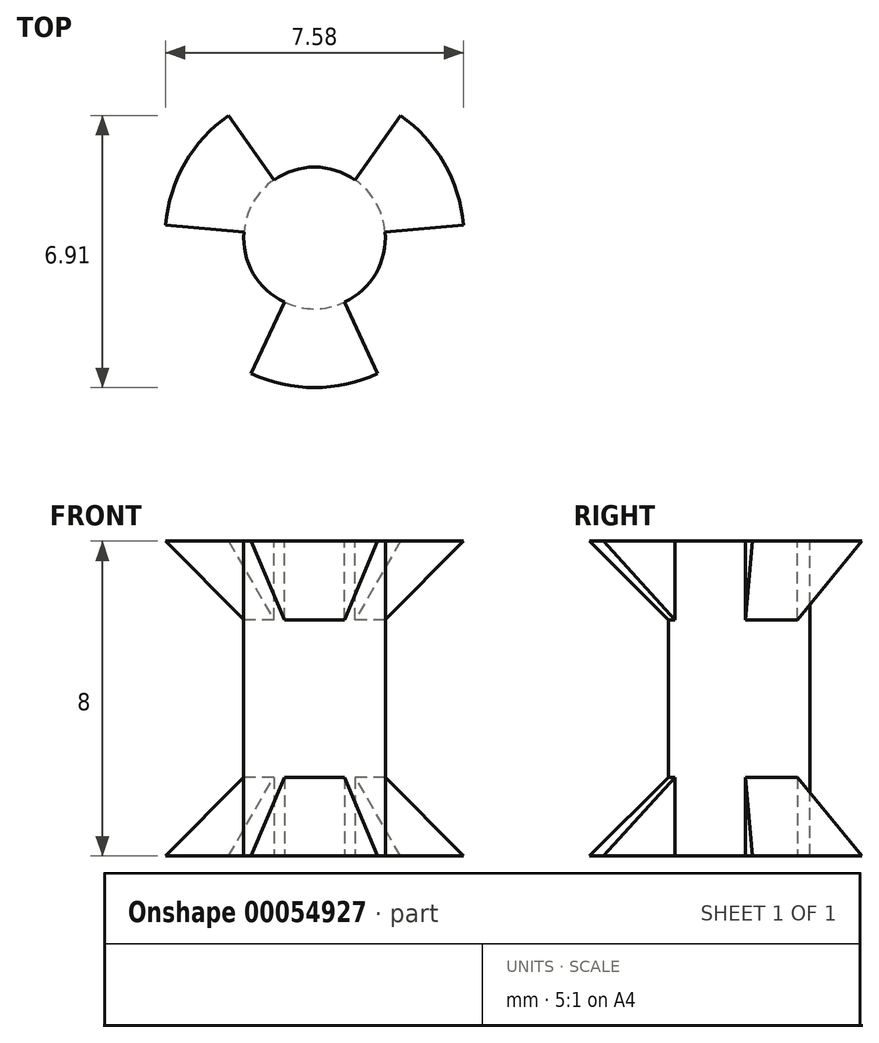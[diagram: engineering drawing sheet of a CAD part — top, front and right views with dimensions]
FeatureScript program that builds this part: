
annotation { "Feature Type Name" : "Feature", "Feature Type Description" : "" }
export const myFeature = defineFeature(function(context is Context, id is Id, definition is map)
    precondition{}
    {
        {
            var Q0;
            Q0=qCreatedBy(makeId("Front.planeOp"),FACE);
            var sketch = newSketch(context, id + "F0", { "sketchPlane" : qUnion([Q0])});
            skLineSegment(sketch, "E0", {"start": v(-1.8, 4) * mm, "end": v(-1.8, 0) * mm});
            skLineSegment(sketch, "E1", {"start": v(-1.8, 4) * mm, "end": v(0, 4) * mm});
            skLineSegment(sketch, "E2", {"start": v(0, 4) * mm, "end": v(0, 0) * mm});
            skLineSegment(sketch, "E3", {"start": v(0, 0) * mm, "end": v(-1.8, 0) * mm});
            skLineSegment(sketch, "E4", {"start": v(-1.8, 0) * mm, "end": v(-3.8, 0) * mm});
            skLineSegment(sketch, "E5", {"start": v(-3.8, 0) * mm, "end": v(-1.8, 2) * mm});
            skPoint(sketch, "E6", {"position": v(-1.8, 2) * mm});
            skSolve(sketch);
        }
        {
            var Q0;
            {var subQ0=sQuery(id+"F0.wireOp",EDGE,"E4");Q0=makeQuery(id+"F0.imprint","IMPRINT",FACE,{"disambiguationData":[TD([[makeQuery(id+"F0.imprint","IMPRINT",EDGE,{"derivedFrom":subQ0}),-1.0]])]});}
            var Q1;
            {var subQ0=sQuery(id+"F0.wireOp",EDGE,"E1");Q1=makeQuery(id+"F0.imprint","IMPRINT",FACE,{"disambiguationData":[TD([[makeQuery(id+"F0.imprint","IMPRINT",EDGE,{"derivedFrom":subQ0}),-1.0]])]});}
            var Q2;
            Q2=sQuery(id+"F0.wireOp",EDGE,"E2");
            revolve(context, id + "F1", {"entities" : qUnion([Q0, Q1]), "axis" : qUnion([Q2]), "revolveType" : RevolveType.FULL});
        }
        {
            var Q0;
            Q0=makeQuery(id+"F1.opRevolve","SWEPT_FACE",FACE,{"disambiguationData":[OSD([sQuery(id+"F0.wireOp",EDGE,"E3"),sQuery(id+"F0.wireOp",EDGE,"E4")])]});
            var sketch = newSketch(context, id + "F2", { "sketchPlane" : qUnion([Q0])});
            skCircle(sketch, "E7.0", {"center": v(0, 0) * mm, "radius": 3.8 * mm});
            skLineSegment(sketch, "E8", {"start": v(-1.6, 3.44) * mm, "end": v(0, 0) * mm});
            skLineSegment(sketch, "E9", {"start": v(1.6, 3.44) * mm, "end": v(0, 0) * mm});
            skLineSegment(sketch, "E10", {"start": v(-3.79, -0.33) * mm, "end": v(0, 0) * mm});
            skLineSegment(sketch, "E11", {"start": v(-2.18, -3.11) * mm, "end": v(0, 0) * mm});
            skLineSegment(sketch, "E12", {"start": v(2.18, -3.11) * mm, "end": v(0, 0) * mm});
            skLineSegment(sketch, "E13", {"start": v(3.79, -0.33) * mm, "end": v(0, 0) * mm});
            skLineSegment(sketch, "E14", {"start": v(0, 3.8) * mm, "end": v(0, 0) * mm, "construction": true});
            skLineSegment(sketch, "E15", {"start": v(0, -3.8) * mm, "end": v(0, 0) * mm, "construction": true});
            skCircle(sketch, "E16.0", {"center": v(0, 0) * mm, "radius": 1.8 * mm});
            skSolve(sketch);
        }
        {
            var Q0;
            {var subQ1=sQuery(id+"F2.wireOp",EDGE,"E10");var subQ3=sQuery(id+"F2.wireOp",EDGE,"E16.0");var subQ4=makeQuery(id+"F2.imprint","INTERSECT",VERTEX,{"derivedFrom":[subQ1,subQ3]});Q0=makeQuery(id+"F2.imprint","IMPRINT",FACE,{"disambiguationData":[TD([[makeQuery(id+"F2.imprint","IMPRINT",EDGE,{"disambiguationData":[TD([[subQ4,-1.0]])],"derivedFrom":subQ3}),1.0]])]});}
            var Q1;
            {var subQ1=sQuery(id+"F2.wireOp",EDGE,"E11");var subQ3=sQuery(id+"F2.wireOp",EDGE,"E16.0");var subQ4=makeQuery(id+"F2.imprint","INTERSECT",VERTEX,{"derivedFrom":[subQ1,subQ3]});Q1=makeQuery(id+"F2.imprint","IMPRINT",FACE,{"disambiguationData":[TD([[makeQuery(id+"F2.imprint","IMPRINT",EDGE,{"disambiguationData":[TD([[subQ4,-1.0]])],"derivedFrom":subQ3}),1.0]])]});}
            var Q2;
            {var subQ1=sQuery(id+"F2.wireOp",EDGE,"E12");var subQ3=sQuery(id+"F2.wireOp",EDGE,"E16.0");var subQ4=makeQuery(id+"F2.imprint","INTERSECT",VERTEX,{"derivedFrom":[subQ1,subQ3]});Q2=makeQuery(id+"F2.imprint","IMPRINT",FACE,{"disambiguationData":[TD([[makeQuery(id+"F2.imprint","IMPRINT",EDGE,{"disambiguationData":[TD([[subQ4,-1.0]])],"derivedFrom":subQ3}),1.0]])]});}
            var Q3;
            {var subQ1=sQuery(id+"F2.wireOp",EDGE,"E9");var subQ3=sQuery(id+"F2.wireOp",EDGE,"E16.0");var subQ4=makeQuery(id+"F2.imprint","INTERSECT",VERTEX,{"derivedFrom":[subQ1,subQ3]});Q3=makeQuery(id+"F2.imprint","IMPRINT",FACE,{"disambiguationData":[TD([[makeQuery(id+"F2.imprint","IMPRINT",EDGE,{"disambiguationData":[TD([[subQ4,1.0]])],"derivedFrom":subQ3}),1.0]])]});}
            var Q4;
            {var subQ1=sQuery(id+"F2.wireOp",EDGE,"E8");var subQ3=sQuery(id+"F2.wireOp",EDGE,"E16.0");var subQ4=makeQuery(id+"F2.imprint","INTERSECT",VERTEX,{"derivedFrom":[subQ1,subQ3]});Q4=makeQuery(id+"F2.imprint","IMPRINT",FACE,{"disambiguationData":[TD([[makeQuery(id+"F2.imprint","IMPRINT",EDGE,{"disambiguationData":[TD([[subQ4,1.0]])],"derivedFrom":subQ3}),1.0]])]});}
            var Q5;
            {var subQ1=sQuery(id+"F2.wireOp",EDGE,"E8");var subQ3=sQuery(id+"F2.wireOp",EDGE,"E16.0");var subQ4=makeQuery(id+"F2.imprint","INTERSECT",VERTEX,{"derivedFrom":[subQ1,subQ3]});Q5=makeQuery(id+"F2.imprint","IMPRINT",FACE,{"disambiguationData":[TD([[makeQuery(id+"F2.imprint","IMPRINT",EDGE,{"disambiguationData":[TD([[subQ4,-1.0]])],"derivedFrom":subQ3}),1.0]])]});}
            var Q6;
            {var subQ0=sQuery(id+"F2.wireOp",EDGE,"E8");var subQ1=sQuery(id+"F2.wireOp",EDGE,"E7.0");var subQ2=makeQuery(id+"F2.imprint","INTERSECT",VERTEX,{"derivedFrom":[subQ1,subQ0]});Q6=makeQuery(id+"F2.imprint","IMPRINT",FACE,{"disambiguationData":[TD([[makeQuery(id+"F2.imprint","IMPRINT",EDGE,{"disambiguationData":[TD([[subQ2,-1.0]])],"derivedFrom":subQ1}),-1.0]])]});}
            var Q7;
            {var subQ0=sQuery(id+"F2.wireOp",EDGE,"E10");var subQ1=sQuery(id+"F2.wireOp",EDGE,"E7.0");var subQ2=makeQuery(id+"F2.imprint","INTERSECT",VERTEX,{"derivedFrom":[subQ1,subQ0]});Q7=makeQuery(id+"F2.imprint","IMPRINT",FACE,{"disambiguationData":[TD([[makeQuery(id+"F2.imprint","IMPRINT",EDGE,{"disambiguationData":[TD([[subQ2,1.0]])],"derivedFrom":subQ1}),-1.0]])]});}
            var Q8;
            {var subQ0=sQuery(id+"F2.wireOp",EDGE,"E12");var subQ1=sQuery(id+"F2.wireOp",EDGE,"E7.0");var subQ2=makeQuery(id+"F2.imprint","INTERSECT",VERTEX,{"derivedFrom":[subQ1,subQ0]});Q8=makeQuery(id+"F2.imprint","IMPRINT",FACE,{"disambiguationData":[TD([[makeQuery(id+"F2.imprint","IMPRINT",EDGE,{"disambiguationData":[TD([[subQ2,1.0]])],"derivedFrom":subQ1}),-1.0]])]});}
            extrude(context, id + "F3", {"entities" : qUnion([Q0, Q1, Q2, Q3, Q4, Q5, Q6, Q7, Q8]), "operationType" : NewBodyOperationType.INTERSECT, "endBound" : BoundingType.THROUGH_ALL, "oppositeDirection" : true, "depth" : 25 * mm});
        }
        {
            var Q0;
            Q0=makeQuery(id+"F1.opRevolve","SWEPT_BODY",BODY,{"disambiguationData":[OSD([sQuery(id+"F0.wireOp",EDGE,"E0"),sQuery(id+"F0.wireOp",EDGE,"E1"),sQuery(id+"F0.wireOp",EDGE,"E2"),sQuery(id+"F0.wireOp",EDGE,"E3"),sQuery(id+"F0.wireOp",EDGE,"E4"),sQuery(id+"F0.wireOp",EDGE,"E5")])]});
            var Q1;
            Q1=makeQuery(id+"F1.opRevolve","SWEPT_FACE",FACE,{"disambiguationData":[OSD([sQuery(id+"F0.wireOp",EDGE,"E1")])]});
            mirror(context, id + "F4", {"operationType" : NewBodyOperationType.ADD, "entities" : qUnion([Q0]), "mirrorPlane" : qUnion([Q1])});
        }
    });
